# Revit family: BE_50565.1_de_DE
name_source: partatom
category: Lighting Fixtures
units: mm (PartAtom-declared; Revit-internal decimal feet)

## family parameters
Cut with Voids When Loaded = Yes
Host = Face
Light Source = Yes
Part Type = Normal
Room Calculation Point = Yes
Round Connector Dimension = Use Diameter
Shared = No

## types (2) — shared parameters
AC/DC = AC/DC
Aktualisierung = 2022-10-27T04:00:03
Apparent Load = 0 VA
BEGA_Dummy = No
BEGA_IES = Yes
BEGA_Intern = Yes
BEGA_Intern_Konstruktion = Yes
BEGA_Intern_an = Yes
BEGA_Intern_aus = Yes
Befestigungsabstand = 96 mm
Befestigungsbohrung = Ø 4,5 mm
Beschreibung_Sonderanfertigung = Hier können Sie Informationen zur Sonderanfertigung eintragen.
CE_Konformität = ja
Color Filter = 16777215
Description = Deckenleuchte
Dimming Lamp Color Temperature Shift = <None>
ENEC = ja
Energieeffizienzklasse = LED A++ - A
Farbwiedergabeindex = CRI > 90
Frequenz = 0/50-60 Hz
Gewicht = 0.95 kg
Lamp = LED 8.1 W
Lastklassifizierung = Beleuchtung
Lebensdauerkriterien = L70B50 @ 25 °C = 200000 h
Logo = <None>
M_A = No
M_G = No
M_W = No
Manufacturer = BEGA
Material_05 = BEGA_Oberfläche_Aluminium_Guss
Material_09 = BEGA_Glas_klar
Material_15 = BEGA_Leuchtmedium_matt
Material_17 = BEGA_Reflektor
Material_34 = BEGA_Oberfläche_Samtweiss_matt
Produktdatenblatt = https://cdn.bega.com
Schutzart = IP 20
Schutzklasse = I
Sonderanfertigung = No
Spannung = 240 V
Tilt Angle = 0.00°
URL = https://www.bega.com
Umgebungstemperatur = 25 °C
zero-valued in all types: Default Elevation

## per-type parameters (varying)
| type | Bestellnummer | Farbtemperatur | LED_Modulbezeichnung | Lampenlichtstrom | Leuchtenlichtstrom | Model | Photometric Web File |
| BEGA_50565.1_K27 | 50565.1K27 | 2700 K | LED-0800/927 | 1200 lm | 943 lm | 50565.1K27 | BE_50565K27.ies |
| BEGA_50565.1_K3 | 50565.1K3 | 3000 K | LED-0800/930 | 1255 lm | 986 lm | 50565.1K3 | BE_50565K3.IES |
